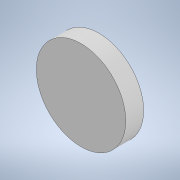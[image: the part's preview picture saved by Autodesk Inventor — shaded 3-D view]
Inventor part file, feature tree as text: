
AUTODESK INVENTOR PART (.ipt)
format: ipt  version: 2021 (Build 250183000, 183)  size: 90,624 bytes
history: native  units: mm
features: extrude x1, sketch x1
ambient origin geometry x8: Origin, YZ Plane, XZ Plane, XY Plane, X Axis, Y Axis, Z Axis, Center Point
bodies: Solid1 (feature_tree)
feature tree (2):
  extrude  "Extrusion1"  Depth=3.0mm TaperAngle=0.0deg
  sketch  "Sketch1"  dims[d0=15.0mm d1=3.0mm d2=0.0mm]
